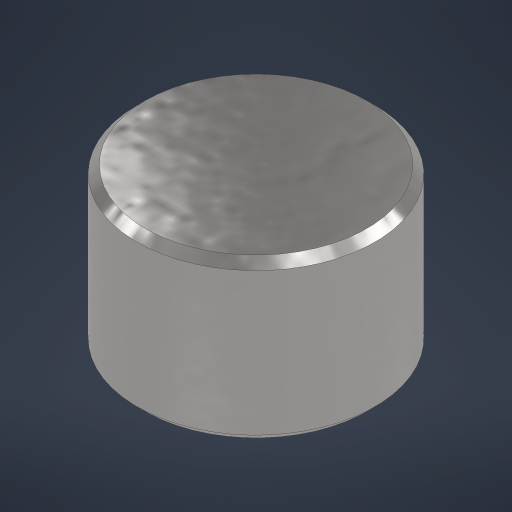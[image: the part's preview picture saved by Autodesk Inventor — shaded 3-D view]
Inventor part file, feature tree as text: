
AUTODESK INVENTOR PART (.ipt)
format: ipt  version: 2024 (Build 280153000, 153)  size: 215,552 bytes
history: native  units: in
note: dims shown in document units (in); Inventor stores cm internally (conversion verified against a paired STEP export)
features: extrude x1, chamfer x1, sketch x1
ambient origin geometry x8: Origin, YZ Plane, XZ Plane, XY Plane, X Axis, Y Axis, Z Axis, Center Point
bodies: Solid1 (feature_tree)
feature tree (3):
  extrude  "Extrusion1"  Depth=0.0787in TaperAngle=0.0deg
  chamfer  "Chamfer1"  Distance=0.0787in Angle=45.0deg
  sketch  "Sketch1"  dims[d0=0.1181in d1=0.0787in d2=0.0in d3=0.0039in d4=0.0787in d5=45.0deg]
